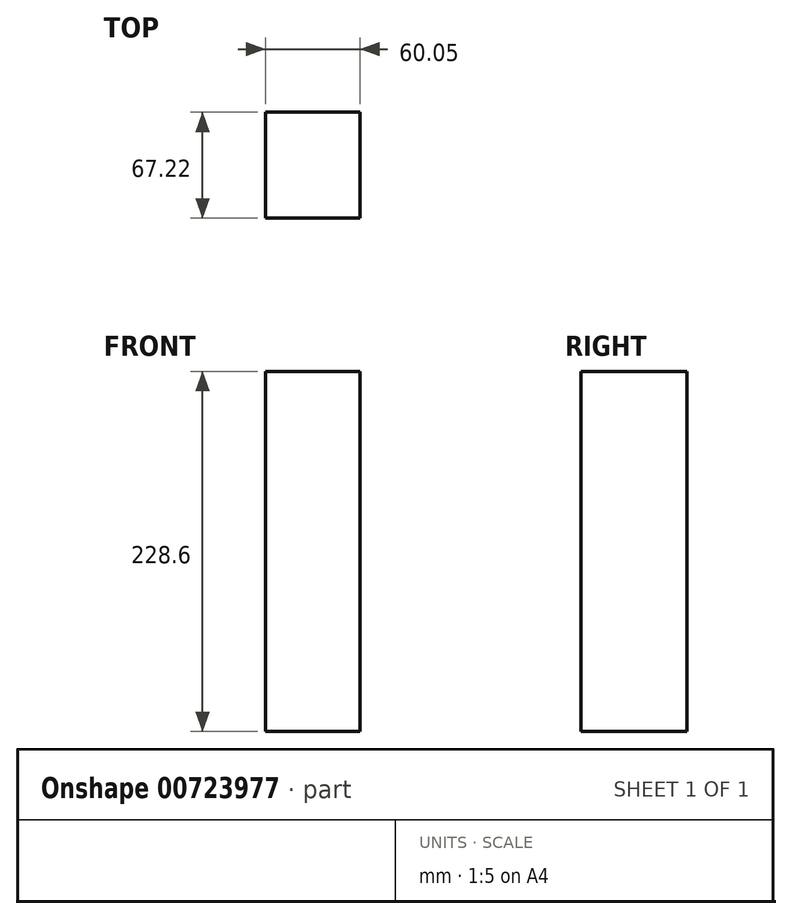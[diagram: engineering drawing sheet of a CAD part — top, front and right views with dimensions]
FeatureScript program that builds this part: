
annotation { "Feature Type Name" : "Feature", "Feature Type Description" : "" }
export const myFeature = defineFeature(function(context is Context, id is Id, definition is map)
    precondition{}
    {
        {
            var Q0;
            Q0=qCreatedBy(makeId("Top.planeOp"),FACE);
            var sketch = newSketch(context, id + "F0", { "sketchPlane" : qUnion([Q0])});
            skLineSegment(sketch, "E0.bottom", {"start": v(69.9, -71.56) * mm, "end": v(9.84, -71.56) * mm});
            skLineSegment(sketch, "E0.top", {"start": v(69.9, -4.34) * mm, "end": v(9.84, -4.34) * mm});
            skLineSegment(sketch, "E0.left", {"start": v(69.9, -71.56) * mm, "end": v(69.9, -4.34) * mm});
            skLineSegment(sketch, "E0.right", {"start": v(9.84, -71.56) * mm, "end": v(9.84, -4.34) * mm});
            skSolve(sketch);
        }
        {
            var Q0;
            Q0 = qSketchRegion(id + "F0", true);
            extrude(context, id + "F1", {"entities" : qUnion([Q0]), "depth" : 228.6 * mm, "offsetDistance" : 25.4 * mm});
        }
    });
